# Revit family: Gaius Under Basin Cabinet_
name_source: partatom
category: Casework
revit_build: Autodesk Revit Architecture 2012 (Build: 20110916_2132(x64)
units: mm (PartAtom-declared; Revit-internal decimal feet)

## types (4) — shared parameters
Height = 800 mm  [stored 2.62467 ft]
Manufacturer = Korpinen Oy
URL = www.korpinen.com
zero-valued in all types: Depth, Width

## per-type parameters (varying)
| type | Cabinet Type | Model |
| 63013 | Under Basin Cabinet : 63013 | 63014 Gaius Under Basin Cabinet with Waste Bin |
| 63014 | Under Basin Cabinet : 63014 | 63014 Gaius Under Basin Cabinet with Waste Bin |
| 63012 | Under Basin Cabinet : 63012 | 63012 Gaius Under Basin Cabinet with Waste Bin |
| 63013  KA | Under Basin Cabinet : 63013 KA | 63013 KA Gaius Under Basin Cabinet with Waste Bin |

note: [stored X ft] marks values corroborated as IEEE doubles in the binary element streams (Revit-internal decimal feet)

## geometry (parser evidence)
native form markers: Sweep x8
no freeform markers — native parametric forms only
